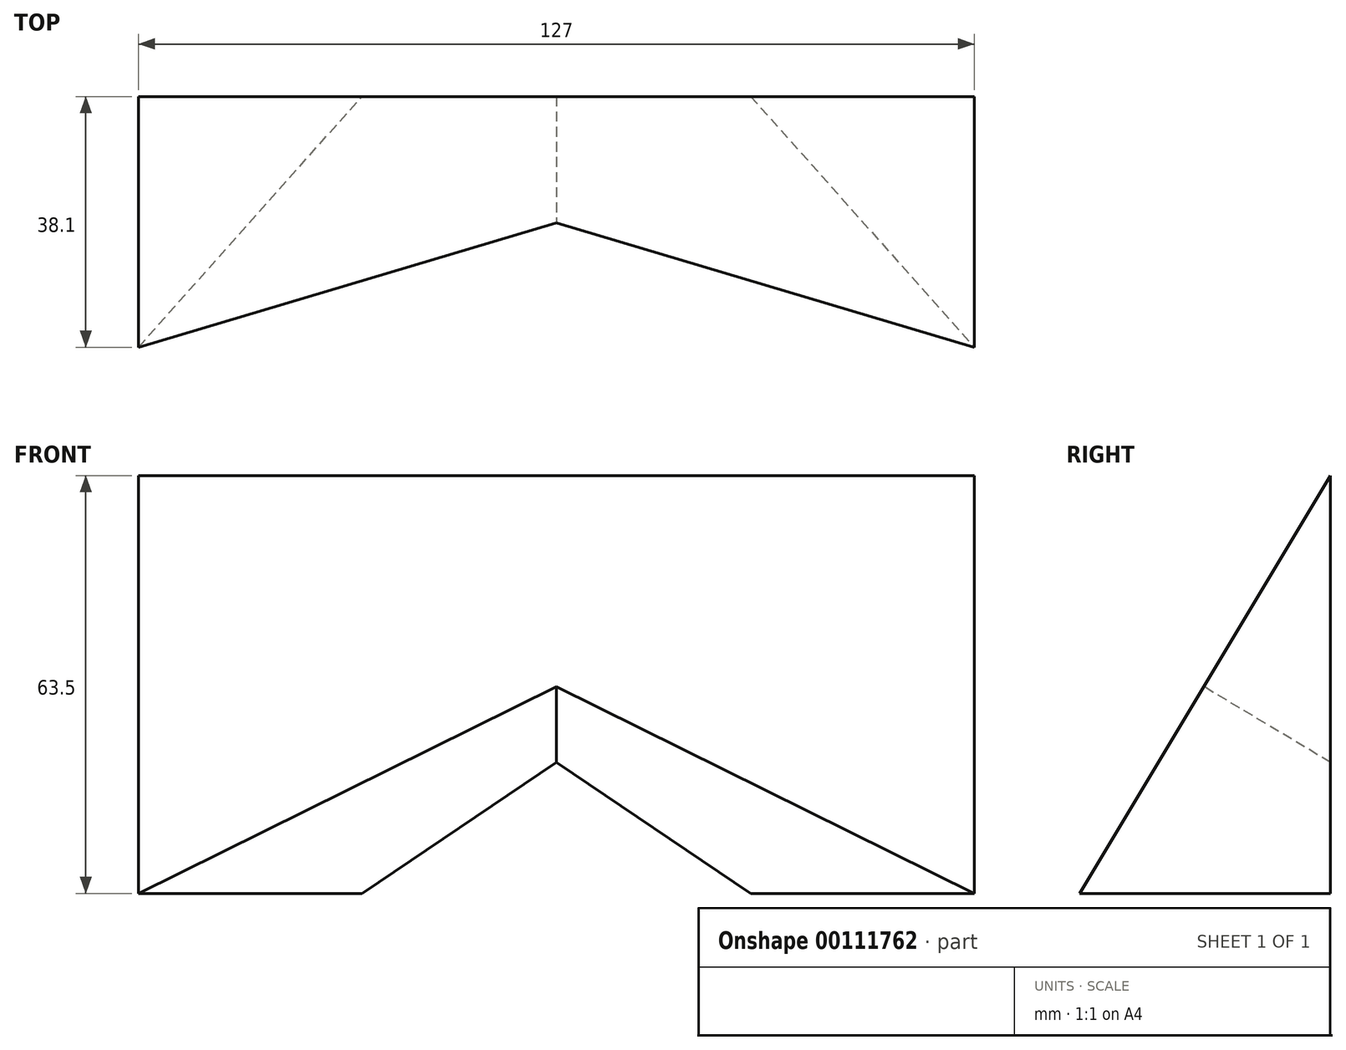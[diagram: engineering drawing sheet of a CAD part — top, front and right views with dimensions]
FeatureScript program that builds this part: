
annotation { "Feature Type Name" : "Feature", "Feature Type Description" : "" }
export const myFeature = defineFeature(function(context is Context, id is Id, definition is map)
    precondition{}
    {
        {
            var Q0;
            Q0=qCreatedBy(makeId("Right.planeOp"),FACE);
            var sketch = newSketch(context, id + "F0", { "sketchPlane" : qUnion([Q0])});
            skLineSegment(sketch, "E0.bottom", {"start": v(-41.47, 41.25) * mm, "end": v(-3.37, 41.25) * mm});
            skLineSegment(sketch, "E0.top", {"start": v(-41.47, -22.25) * mm, "end": v(-3.37, -22.25) * mm});
            skLineSegment(sketch, "E0.left", {"start": v(-41.47, 41.25) * mm, "end": v(-41.47, -22.25) * mm});
            skLineSegment(sketch, "E0.right", {"start": v(-3.37, 41.25) * mm, "end": v(-3.37, -22.25) * mm});
            skLineSegment(sketch, "E1", {"start": v(-3.37, 41.25) * mm, "end": v(-41.47, -22.25) * mm});
            skSolve(sketch);
        }
        {
            var Q0;
            Q0=makeQuery(id+"F0.imprint","IMPRINT",FACE,{"disambiguationData":[TD([[makeQuery(id+"F0.imprint","IMPRINT",EDGE,{"derivedFrom":sQuery(id+"F0.wireOp",EDGE,"E0.top")}),1.0]])]});
            extrude(context, id + "F1", {"entities" : qUnion([Q0]), "oppositeDirection" : true, "depth" : 127 * mm});
        }
        {
            var Q0;
            Q0=makeQuery(id+"F1.opExtrude","SWEPT_FACE",FACE,{"disambiguationData":[OSD([sQuery(id+"F0.wireOp",EDGE,"E1")])]});
            var sketch = newSketch(context, id + "F2", { "sketchPlane" : qUnion([Q0])});
            skLineSegment(sketch, "E2", {"start": v(0, -40.42) * mm, "end": v(-63.5, -3.75) * mm});
            skPoint(sketch, "E2.endSnap0", {"position": v(-63.5, 33.64) * mm});
            skLineSegment(sketch, "E3", {"start": v(-63.5, -3.75) * mm, "end": v(-127, -40.42) * mm});
            skSolve(sketch);
        }
        {
            var Q0;
            Q0 = qSketchRegion(id + "F2", true);
            var Q1;
            Q1=makeQuery(id+"F2.imprint","IMPRINT",FACE,{"disambiguationData":[TD([[makeQuery(id+"F2.imprint","IMPRINT",EDGE,{"derivedFrom":sQuery(id+"F2.wireOp",EDGE,"E2")}),1.0]])]});
            extrude(context, id + "F3", {"entities" : qUnion([Q0, Q1]), "operationType" : NewBodyOperationType.REMOVE, "endBound" : BoundingType.THROUGH_ALL, "oppositeDirection" : true, "depth" : 25.4 * mm});
        }
    });
